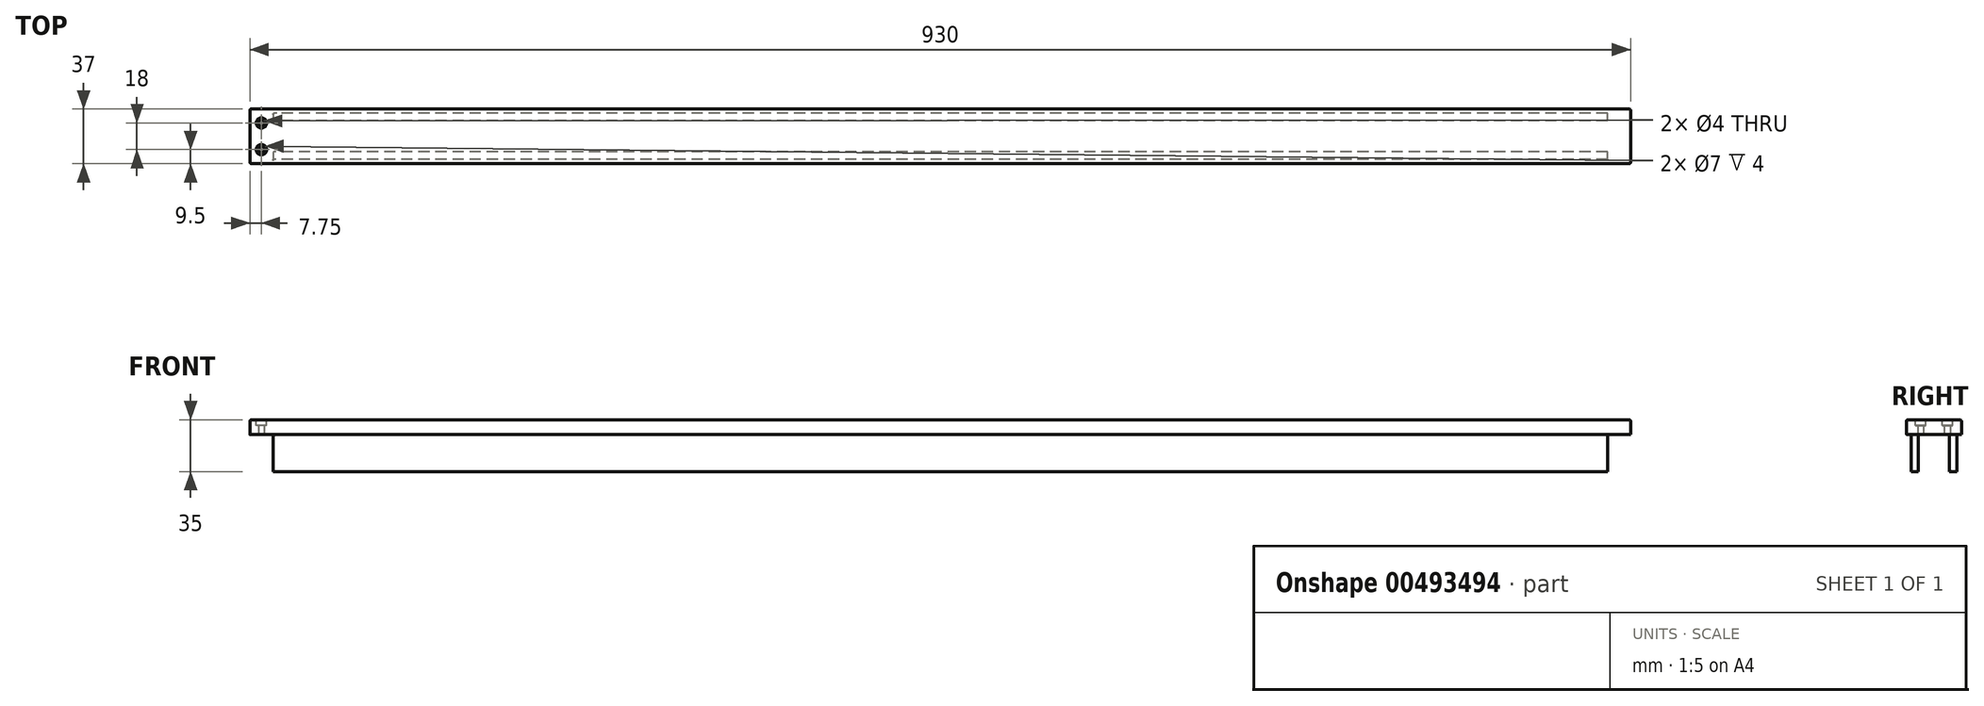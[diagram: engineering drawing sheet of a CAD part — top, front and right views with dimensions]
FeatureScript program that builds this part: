
annotation { "Feature Type Name" : "Feature", "Feature Type Description" : "" }
export const myFeature = defineFeature(function(context is Context, id is Id, definition is map)
    precondition{}
    {
        {
            var Q0;
            Q0=qCreatedBy(makeId("Right.planeOp"),FACE);
            var sketch = newSketch(context, id + "F0", { "sketchPlane" : qUnion([Q0])});
            skLineSegment(sketch, "E0", {"start": v(0, 60.8) * mm, "end": v(0, -55.58) * mm, "construction": true});
            skLineSegment(sketch, "E1", {"start": v(66.15, 0) * mm, "end": v(-54.47, 0) * mm, "construction": true});
            skLineSegment(sketch, "E2.bottom", {"start": v(-18.5, 12.5) * mm, "end": v(18.5, 12.5) * mm});
            skLineSegment(sketch, "E2.top", {"start": v(-15.5, -22.5) * mm, "end": v(-10.5, -22.5) * mm});
            skLineSegment(sketch, "E2.left", {"start": v(-18.5, 12.5) * mm, "end": v(-18.5, 2.5) * mm});
            skLineSegment(sketch, "E2.right", {"start": v(18.5, 12.5) * mm, "end": v(18.5, 0) * mm, "construction": true});
            skLineSegment(sketch, "E3", {"start": v(-18.5, 2.5) * mm, "end": v(-15.5, 2.5) * mm});
            skLineSegment(sketch, "E4", {"start": v(-15.5, 2.5) * mm, "end": v(-15.5, -22.5) * mm});
            skLineSegment(sketch, "E5", {"start": v(-10.5, -22.5) * mm, "end": v(-10.5, 2.5) * mm});
            skLineSegment(sketch, "E6", {"start": v(-10.5, 2.5) * mm, "end": v(0, 2.5) * mm});
            skLineSegment(sketch, "E7.MirrorCS", {"start": v(10.5, 2.5) * mm, "end": v(0, 2.5) * mm});
            skLineSegment(sketch, "E8.MirrorCS", {"start": v(10.5, -22.5) * mm, "end": v(10.5, 2.5) * mm});
            skLineSegment(sketch, "E9.MirrorCS", {"start": v(15.5, 2.5) * mm, "end": v(15.5, -22.5) * mm});
            skLineSegment(sketch, "E10.MirrorCS", {"start": v(15.5, -22.5) * mm, "end": v(10.5, -22.5) * mm});
            skLineSegment(sketch, "E11.MirrorCS", {"start": v(18.5, 2.5) * mm, "end": v(15.5, 2.5) * mm});
            skLineSegment(sketch, "E12", {"start": v(18.5, 2.5) * mm, "end": v(18.5, 12.5) * mm});
            skSolve(sketch);
        }
        {
            var Q0;
            Q0=qSketchRegion(id+"F0",true);
            extrude(context, id + "F1", {"entities" : qUnion([Q0]), "depth" : 930 * mm, "symmetric" : true});
        }
        {
            var Q0;
            Q0=makeQuery(id+"F1.opExtrude","CAP_FACE",FACE,{"disambiguationData":[OSD([sQuery(id+"F0.wireOp",EDGE,"E2.bottom"),sQuery(id+"F0.wireOp",EDGE,"E2.top"),sQuery(id+"F0.wireOp",EDGE,"E2.left"),sQuery(id+"F0.wireOp",EDGE,"E3"),sQuery(id+"F0.wireOp",EDGE,"E4"),sQuery(id+"F0.wireOp",EDGE,"E5"),sQuery(id+"F0.wireOp",EDGE,"E6"),sQuery(id+"F0.wireOp",EDGE,"E7.MirrorCS"),sQuery(id+"F0.wireOp",EDGE,"E8.MirrorCS"),sQuery(id+"F0.wireOp",EDGE,"E9.MirrorCS"),sQuery(id+"F0.wireOp",EDGE,"E10.MirrorCS"),sQuery(id+"F0.wireOp",EDGE,"E11.MirrorCS"),sQuery(id+"F0.wireOp",EDGE,"E12")])],"isStart":true});
            var sketch = newSketch(context, id + "F2", { "sketchPlane" : qUnion([Q0])});
            skLineSegment(sketch, "E13.bottom", {"start": v(-15.5, 2.5) * mm, "end": v(15.5, 2.5) * mm});
            skLineSegment(sketch, "E13.top", {"start": v(-15.5, -22.5) * mm, "end": v(15.5, -22.5) * mm});
            skLineSegment(sketch, "E13.left", {"start": v(-15.5, 2.5) * mm, "end": v(-15.5, -22.5) * mm});
            skLineSegment(sketch, "E13.right", {"start": v(15.5, 2.5) * mm, "end": v(15.5, -22.5) * mm});
            skSolve(sketch);
        }
        {
            var Q0;
            Q0=qSketchRegion(id+"F2",true);
            extrude(context, id + "F3", {"entities" : qUnion([Q0]), "operationType" : NewBodyOperationType.REMOVE, "oppositeDirection" : true, "depth" : 15.5 * mm});
        }
        {
            var Q0;
            Q0=makeQuery(id+"F1.opExtrude","CAP_FACE",FACE,{"disambiguationData":[OSD([sQuery(id+"F0.wireOp",EDGE,"E2.bottom"),sQuery(id+"F0.wireOp",EDGE,"E2.top"),sQuery(id+"F0.wireOp",EDGE,"E2.left"),sQuery(id+"F0.wireOp",EDGE,"E3"),sQuery(id+"F0.wireOp",EDGE,"E4"),sQuery(id+"F0.wireOp",EDGE,"E5"),sQuery(id+"F0.wireOp",EDGE,"E6"),sQuery(id+"F0.wireOp",EDGE,"E7.MirrorCS"),sQuery(id+"F0.wireOp",EDGE,"E8.MirrorCS"),sQuery(id+"F0.wireOp",EDGE,"E9.MirrorCS"),sQuery(id+"F0.wireOp",EDGE,"E10.MirrorCS"),sQuery(id+"F0.wireOp",EDGE,"E11.MirrorCS"),sQuery(id+"F0.wireOp",EDGE,"E12")])],"isStart":false});
            var sketch = newSketch(context, id + "F4", { "sketchPlane" : qUnion([Q0])});
            skLineSegment(sketch, "E14.bottom", {"start": v(-15.5, 2.5) * mm, "end": v(15.5, 2.5) * mm});
            skLineSegment(sketch, "E14.top", {"start": v(-15.5, -22.5) * mm, "end": v(15.5, -22.5) * mm});
            skLineSegment(sketch, "E14.left", {"start": v(-15.5, 2.5) * mm, "end": v(-15.5, -22.5) * mm});
            skLineSegment(sketch, "E14.right", {"start": v(15.5, 2.5) * mm, "end": v(15.5, -22.5) * mm});
            skSolve(sketch);
        }
        {
            var Q0;
            Q0=qSketchRegion(id+"F4",true);
            extrude(context, id + "F5", {"entities" : qUnion([Q0]), "operationType" : NewBodyOperationType.REMOVE, "oppositeDirection" : true, "depth" : 15.5 * mm});
        }
        {
            var Q0;
            Q0=makeQuery(id+"F5.boolean.opBoolean","MERGE",FACE,{"derivedFrom":[makeQuery(id+"F3.boolean.opBoolean","MERGE",FACE,{"derivedFrom":[makeQuery(id+"F1.opExtrude","SWEPT_FACE",FACE,{"disambiguationData":[OSD([sQuery(id+"F0.wireOp",EDGE,"E3")])]}),makeQuery(id+"F1.opExtrude","SWEPT_FACE",FACE,{"disambiguationData":[OSD([sQuery(id+"F0.wireOp",EDGE,"E6"),sQuery(id+"F0.wireOp",EDGE,"E7.MirrorCS")])]}),makeQuery(id+"F1.opExtrude","SWEPT_FACE",FACE,{"disambiguationData":[OSD([sQuery(id+"F0.wireOp",EDGE,"E11.MirrorCS")])]}),makeQuery(id+"F3.opExtrude","SWEPT_FACE",FACE,{"disambiguationData":[OSD([sQuery(id+"F2.wireOp",EDGE,"E13.bottom")])]})]}),makeQuery(id+"F5.opExtrude","SWEPT_FACE",FACE,{"disambiguationData":[OSD([sQuery(id+"F4.wireOp",EDGE,"E14.bottom")])]})]});
            var sketch = newSketch(context, id + "F6", { "sketchPlane" : qUnion([Q0])});
            skLineSegment(sketch, "E15", {"start": v(-449.5, 15.5) * mm, "end": v(-449.5, -15.5) * mm, "construction": true});
            skLineSegment(sketch, "E16", {"start": v(-449.5, 0) * mm, "end": v(-465, 0) * mm, "construction": true});
            skLineSegment(sketch, "E17", {"start": v(-457.25, 0) * mm, "end": v(-457.25, 18.5) * mm, "construction": true});
            skCircle(sketch, "E18", {"center": v(-457.25, 9) * mm, "radius": 2 * mm});
            skCircle(sketch, "E19.MirrorC", {"center": v(-457.25, -9) * mm, "radius": 2 * mm});
            skSolve(sketch);
        }
        {
            var Q0;
            Q0=qSketchRegion(id+"F6",true);
            extrude(context, id + "F7", {"entities" : qUnion([Q0]), "operationType" : NewBodyOperationType.REMOVE, "endBound" : BoundingType.THROUGH_ALL, "oppositeDirection" : true, "depth" : 25 * mm});
        }
        {
            var Q0;
            Q0=makeQuery(id+"F1.opExtrude","SWEPT_FACE",FACE,{"disambiguationData":[OSD([sQuery(id+"F0.wireOp",EDGE,"E2.bottom")])]});
            var sketch = newSketch(context, id + "F8", { "sketchPlane" : qUnion([Q0])});
            skCircle(sketch, "E20.0", {"center": v(-457.25, -9) * mm, "radius": 3.5 * mm});
            skCircle(sketch, "E21.0", {"center": v(-457.25, 9) * mm, "radius": 3.5 * mm});
            skLineSegment(sketch, "E22", {"start": v(-460.75, -9) * mm, "end": v(-465, -9) * mm, "construction": true});
            skSolve(sketch);
        }
        {
            var Q0;
            Q0=qSketchRegion(id+"F8",true);
            extrude(context, id + "F9", {"entities" : qUnion([Q0]), "operationType" : NewBodyOperationType.REMOVE, "oppositeDirection" : true, "depth" : 4 * mm});
        }
        {
            var Q0;
            Q0=makeQuery(id+"F1.opExtrude","CAP_EDGE",EDGE,{"disambiguationData":[OSD([sQuery(id+"F0.wireOp",EDGE,"E12")])],"isStart":false});
            var Q1;
            Q1=makeQuery(id+"F1.opExtrude","CAP_EDGE",EDGE,{"disambiguationData":[OSD([sQuery(id+"F0.wireOp",EDGE,"E2.left")])],"isStart":false});
            var Q2;
            {var subQ0=sQuery(id+"F4.wireOp",EDGE,"E14.top");Q2=makeQuery(id+"F5.boolean.opBoolean","COPY",EDGE,{"disambiguationData":[topologyDisambiguationEdgeConnected([makeQuery(id+"F1.opExtrude","SWEPT_FACE",FACE,{"disambiguationData":[OSD([sQuery(id+"F0.wireOp",EDGE,"E10.MirrorCS")])]})])],"derivedFrom":makeQuery(id+"F5.opExtrude","CAP_EDGE",EDGE,{"disambiguationData":[OSD([subQ0])],"isStart":false})});}
            var Q3;
            {var subQ0=sQuery(id+"F4.wireOp",EDGE,"E14.top");Q3=makeQuery(id+"F5.boolean.opBoolean","COPY",EDGE,{"disambiguationData":[topologyDisambiguationEdgeConnected([makeQuery(id+"F1.opExtrude","SWEPT_FACE",FACE,{"disambiguationData":[OSD([sQuery(id+"F0.wireOp",EDGE,"E2.top")])]})])],"derivedFrom":makeQuery(id+"F5.opExtrude","CAP_EDGE",EDGE,{"disambiguationData":[OSD([subQ0])],"isStart":false})});}
            var Q4;
            Q4=makeQuery(id+"F1.opExtrude","CAP_EDGE",EDGE,{"disambiguationData":[OSD([sQuery(id+"F0.wireOp",EDGE,"E2.left")])],"isStart":true});
            var Q5;
            {var subQ0=sQuery(id+"F2.wireOp",EDGE,"E13.top");Q5=makeQuery(id+"F3.boolean.opBoolean","COPY",EDGE,{"disambiguationData":[topologyDisambiguationEdgeConnected([makeQuery(id+"F1.opExtrude","SWEPT_FACE",FACE,{"disambiguationData":[OSD([sQuery(id+"F0.wireOp",EDGE,"E2.top")])]})])],"derivedFrom":makeQuery(id+"F3.opExtrude","CAP_EDGE",EDGE,{"disambiguationData":[OSD([subQ0])],"isStart":false})});}
            var Q6;
            {var subQ0=sQuery(id+"F2.wireOp",EDGE,"E13.top");Q6=makeQuery(id+"F3.boolean.opBoolean","COPY",EDGE,{"disambiguationData":[topologyDisambiguationEdgeConnected([makeQuery(id+"F1.opExtrude","SWEPT_FACE",FACE,{"disambiguationData":[OSD([sQuery(id+"F0.wireOp",EDGE,"E10.MirrorCS")])]})])],"derivedFrom":makeQuery(id+"F3.opExtrude","CAP_EDGE",EDGE,{"disambiguationData":[OSD([subQ0])],"isStart":false})});}
            var Q7;
            Q7=makeQuery(id+"F1.opExtrude","CAP_EDGE",EDGE,{"disambiguationData":[OSD([sQuery(id+"F0.wireOp",EDGE,"E12")])],"isStart":true});
            fillet(context, id + "F10", {"entities" : qUnion([Q0, Q1, Q2, Q3, Q4, Q5, Q6, Q7]), "radius" : 1 * mm, "tangentPropagation" : true, "allowEdgeOverflow" : false});
        }
        {
            var Q0;
            Q0=makeQuery(id+"F3.boolean.opBoolean","INTERSECT",EDGE,{"derivedFrom":[makeQuery(id+"F1.opExtrude","SWEPT_FACE",FACE,{"disambiguationData":[OSD([sQuery(id+"F0.wireOp",EDGE,"E5")])]}),makeQuery(id+"F3.opExtrude","CAP_FACE",FACE,{"disambiguationData":[OSD([sQuery(id+"F2.wireOp",EDGE,"E13.bottom"),sQuery(id+"F2.wireOp",EDGE,"E13.top"),sQuery(id+"F2.wireOp",EDGE,"E13.left"),sQuery(id+"F2.wireOp",EDGE,"E13.right")])],"isStart":false})]});
            var Q1;
            Q1=makeQuery(id+"F3.boolean.opBoolean","COPY",EDGE,{"derivedFrom":makeQuery(id+"F3.opExtrude","CAP_EDGE",EDGE,{"disambiguationData":[OSD([sQuery(id+"F2.wireOp",EDGE,"E13.right")])],"isStart":false})});
            var Q2;
            Q2=makeQuery(id+"F3.boolean.opBoolean","COPY",EDGE,{"derivedFrom":makeQuery(id+"F3.opExtrude","CAP_EDGE",EDGE,{"disambiguationData":[OSD([sQuery(id+"F2.wireOp",EDGE,"E13.left")])],"isStart":false})});
            var Q3;
            {var subQ0=sQuery(id+"F2.wireOp",EDGE,"E13.bottom");Q3=makeQuery(id+"F3.boolean.opBoolean","COPY",FACE,{"disambiguationData":[TD([makeQuery(id+"F1.opExtrude","SWEPT_FACE",FACE,{"disambiguationData":[OSD([sQuery(id+"F0.wireOp",EDGE,"E8.MirrorCS")])]})])],"derivedFrom":makeQuery(id+"F3.opExtrude","CAP_FACE",FACE,{"disambiguationData":[OSD([subQ0,sQuery(id+"F2.wireOp",EDGE,"E13.top"),sQuery(id+"F2.wireOp",EDGE,"E13.left"),sQuery(id+"F2.wireOp",EDGE,"E13.right")])],"isStart":false})});}
            var Q4;
            Q4=makeQuery(id+"F3.boolean.opBoolean","MERGE",EDGE,{"derivedFrom":[makeQuery(id+"F1.opExtrude","CAP_EDGE",EDGE,{"disambiguationData":[OSD([sQuery(id+"F0.wireOp",EDGE,"E3")])],"isStart":true}),makeQuery(id+"F1.opExtrude","CAP_EDGE",EDGE,{"disambiguationData":[OSD([sQuery(id+"F0.wireOp",EDGE,"E6"),sQuery(id+"F0.wireOp",EDGE,"E7.MirrorCS")])],"isStart":true}),makeQuery(id+"F1.opExtrude","CAP_EDGE",EDGE,{"disambiguationData":[OSD([sQuery(id+"F0.wireOp",EDGE,"E11.MirrorCS")])],"isStart":true}),makeQuery(id+"F3.opExtrude","CAP_EDGE",EDGE,{"disambiguationData":[OSD([sQuery(id+"F2.wireOp",EDGE,"E13.bottom")])],"isStart":true})]});
            var Q5;
            Q5=makeQuery(id+"F1.opExtrude","CAP_EDGE",EDGE,{"disambiguationData":[OSD([sQuery(id+"F0.wireOp",EDGE,"E2.bottom")])],"isStart":true});
            var Q6;
            Q6=makeQuery(id+"F1.opExtrude","SWEPT_EDGE",EDGE,{"disambiguationData":[OSD([sQuery(id+"F0.wireOp",EDGE,"E3"),sQuery(id+"F0.wireOp",EDGE,"E4")])]});
            fillet(context, id + "F11", {"entities" : qUnion([Q0, Q1, Q2, Q3, Q4, Q5, Q6]), "radius" : 1 * mm, "tangentPropagation" : true, "allowEdgeOverflow" : false});
        }
    });
